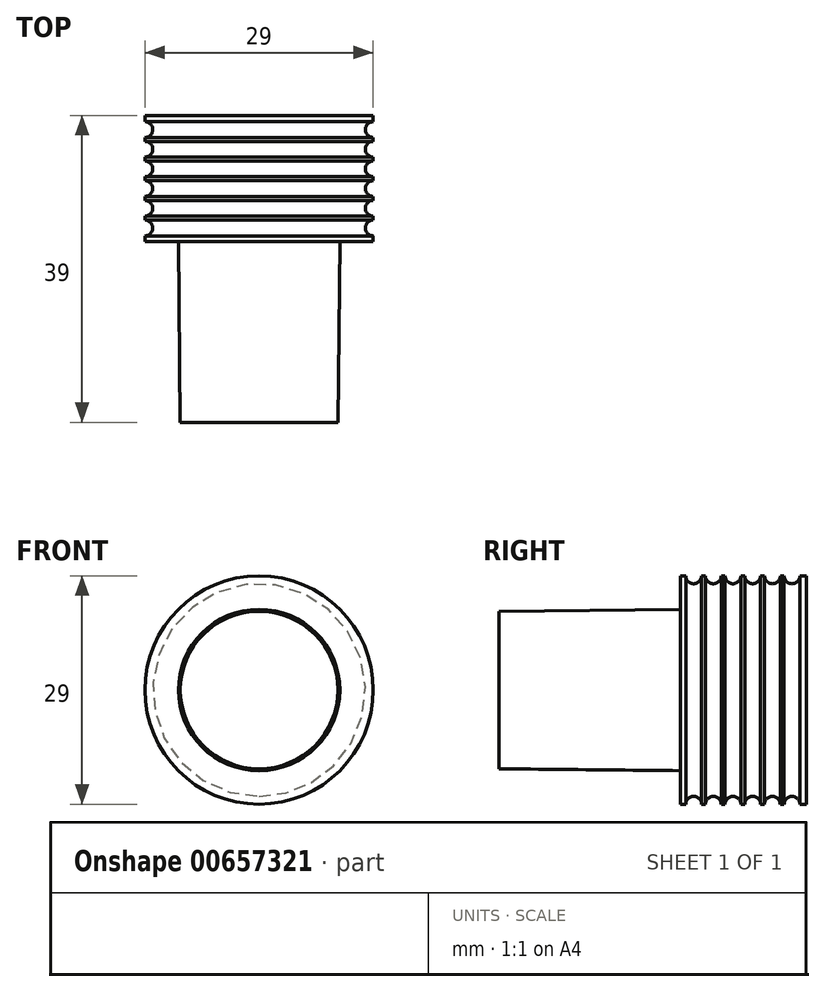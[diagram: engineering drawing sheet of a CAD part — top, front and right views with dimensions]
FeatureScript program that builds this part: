
annotation { "Feature Type Name" : "Feature", "Feature Type Description" : "" }
export const myFeature = defineFeature(function(context is Context, id is Id, definition is map)
    precondition{}
    {
        {
            var Q0;
            Q0=qCreatedBy(makeId("Front.planeOp"),FACE);
            var sketch = newSketch(context, id + "F0", { "sketchPlane" : qUnion([Q0])});
            skCircle(sketch, "E0", {"center": v(0, 0) * mm, "radius": 14.5 * mm});
            skSolve(sketch);
        }
        {
            var Q0;
            Q0 = qSketchRegion(id + "F0", true);
            extrude(context, id + "F1", {"entities" : qUnion([Q0]), "depth" : 16 * mm, "offsetDistance" : 25 * mm});
        }
        {
            var Q0;
            Q0=makeQuery(id+"F1.opExtrude","CAP_FACE",FACE,{"disambiguationData":[OSD([sQuery(id+"F0.wireOp",EDGE,"E0")])],"isStart":false});
            var sketch = newSketch(context, id + "F2", { "sketchPlane" : qUnion([Q0])});
            skCircle(sketch, "E1", {"center": v(0, 0) * mm, "radius": 10.25 * mm});
            skSolve(sketch);
        }
        {
            var Q0;
            Q0 = qSketchRegion(id + "F2", true);
            extrude(context, id + "F3", {"entities" : qUnion([Q0]), "operationType" : NewBodyOperationType.ADD, "depth" : 23 * mm, "offsetDistance" : 25 * mm, "hasDraft" : true, "draftAngle" : 0.6 * degree, "draftPullDirection" : true});
        }
        {
            var Q0;
            Q0=qCreatedBy(makeId("Top.planeOp"),FACE);
            var sketch = newSketch(context, id + "F4", { "sketchPlane" : qUnion([Q0])});
            skLineSegment(sketch, "E2", {"start": v(-14.5, 0) * mm, "end": v(-14.5, -16) * mm});
            skCircle(sketch, "E3", {"center": v(-14.5, -1.8) * mm, "radius": 1 * mm});
            skCircle(sketch, "E4", {"center": v(-14.5, -4.3) * mm, "radius": 1 * mm});
            skCircle(sketch, "E5", {"center": v(-14.5, -6.8) * mm, "radius": 1 * mm});
            skCircle(sketch, "E6", {"center": v(-14.5, -9.3) * mm, "radius": 1 * mm});
            skCircle(sketch, "E7", {"center": v(-14.5, -11.8) * mm, "radius": 1 * mm});
            skCircle(sketch, "E8", {"center": v(-14.5, -14.3) * mm, "radius": 1 * mm});
            skLineSegment(sketch, "E9", {"start": v(0, 0) * mm, "end": v(0, -44.47) * mm, "construction": true});
            skSolve(sketch);
        }
        {
            var Q0;
            Q0 = qSketchRegion(id + "F4", true);
            var Q1;
            Q1=sQuery(id+"F4.wireOp",EDGE,"E9");
            revolve(context, id + "F5", {"operationType" : NewBodyOperationType.REMOVE, "entities" : qUnion([Q0]), "axis" : qUnion([Q1]), "revolveType" : RevolveType.FULL, "oppositeDirection" : true});
        }
    });
